# Revit family: SOLID EXIT 2 LED EMERGENCY EXIT LIGHT TWT3151WK
name_source: partatom
category: Lighting Fixtures
revit_build: Autodesk Revit 2015 (Build: 20160512_0715(x64)
units: mm (PartAtom-declared; Revit-internal decimal feet)

## types (4) — shared parameters
Color = RAL9003
Default Elevation = 1219 mm
Depth = 181 mm  [stored 0.593832 ft]
Height = 232 mm  [stored 0.761155 ft]
Manufacturer = Teknoware Oy
Material = Plastic
Model = Solid Exit 2
Product Code = TWT3151WK
Width = 371 mm  [stored 1.21719 ft]

## per-type parameters (varying)
| type | Back Pictogram | Down | Front Pictogram | Left | Right | Type Comments | Up |
| -arrow down | Teknoware Pictogram PBV31302E3 | Yes | Teknoware Pictogram PBV31302E3 | No | No | PBV31302E3 | No |
| -arrow up | Teknoware Pictogram PBV31305E3 | No | Teknoware Pictogram PBV31305E3 | No | No | PBV31305E3 | Yes |
| -arrow left | Teknoware Pictogram PBV31301E1 | No | Teknoware Pictogram PBV31301E2 | Yes | No | PBV31301E2 | No |
| -arrow right | Teknoware Pictogram PBV31301E2 | No | Teknoware Pictogram PBV31301E1 | No | Yes | PBV31301E1 | No |

note: [stored X ft] marks values corroborated as IEEE doubles in the binary element streams (Revit-internal decimal feet)

## geometry (parser evidence)
native form markers: Blend x8, Sweep x13
no freeform markers — native parametric forms only
